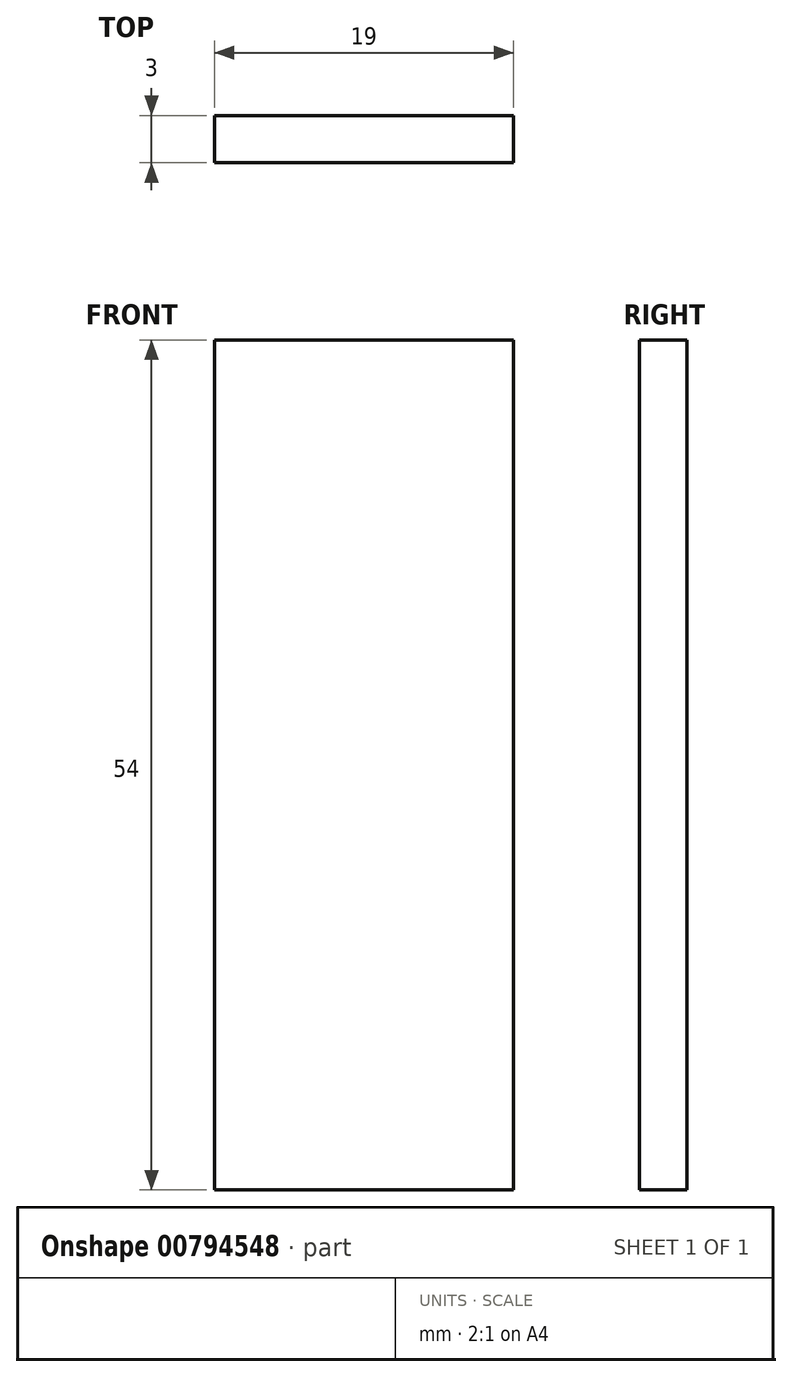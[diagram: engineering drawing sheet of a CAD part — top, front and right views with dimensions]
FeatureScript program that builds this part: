
annotation { "Feature Type Name" : "Feature", "Feature Type Description" : "" }
export const myFeature = defineFeature(function(context is Context, id is Id, definition is map)
    precondition{}
    {
        {
            var Q0;
            Q0=qCreatedBy(makeId("Front.planeOp"),FACE);
            var sketch = newSketch(context, id + "F0", { "sketchPlane" : qUnion([Q0])});
            skLineSegment(sketch, "E0.bottom", {"start": v(-9.5, 27) * mm, "end": v(9.5, 27) * mm});
            skLineSegment(sketch, "E0.top", {"start": v(-9.5, -27) * mm, "end": v(9.5, -27) * mm});
            skLineSegment(sketch, "E0.left", {"start": v(-9.5, 27) * mm, "end": v(-9.5, -27) * mm});
            skLineSegment(sketch, "E0.right", {"start": v(9.5, 27) * mm, "end": v(9.5, -27) * mm});
            skPoint(sketch, "E0.middle", {"position": v(0, 0) * mm});
            skSolve(sketch);
        }
        {
            var Q0;
            Q0=makeQuery(id+"F0.imprint","IMPRINT",FACE,{"disambiguationData":[TD([[makeQuery(id+"F0.imprint","IMPRINT",EDGE,{"derivedFrom":sQuery(id+"F0.wireOp",EDGE,"E0.bottom")}),-1.0]])]});
            extrude(context, id + "F1", {"entities" : qUnion([Q0]), "depth" : 3 * mm, "offsetDistance" : 25 * mm});
        }
    });
